# Revit family: Outdoor-Kitchen-Equipment_Kalamazoo_Artisan-Countertop-Pizza-Oven1
name_source: partatom
category: Specialty Equipment
revit_build: Autodesk Revit 2018 (Build: 20190510_1515(x64)
units: mm (PartAtom-declared; Revit-internal decimal feet)

## family parameters
Cut with Voids When Loaded = No
Host = Face
OmniClass Number = 23.40.40.14.17.31
OmniClass Title = Small Specialized Cooking Equipment
Part Type = Normal
Room Calculation Point = No
Round Connector Dimension = Use Diameter
Shared = No

## types (1)
- AFPO-C
    Assembly Code = E1090320
    Default Elevation = 48"
    Depth = 30"
    Description = Countertop Artisan Fire Pizza Oven
    Fuel Type = Natural Gas
    Gas Connection Size = 0"
    Gas Flow = 0 GPM
    Height = 19 1/2"
    Keynote = 11400
    Liquid Propane = No
    Manufacturer = Kalamazoo Outdoor Gourmet
    Model = AFPO-C
    Natural Gas = Yes
    Product Material = Kalamazoo - Stainless Steel - 304 OR 316L
    Product data url = https://www.bimobject.com
    Total Heating Capacity = 43500.0 Btu/h
    URL = https://kalamazoogourmet.com
    Weight (lb) = 130.00 lbf
    Width = 30 1/8"

## geometry (parser evidence)
native form markers: Sweep x4
no freeform markers — native parametric forms only
